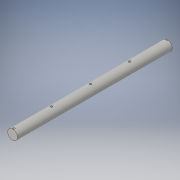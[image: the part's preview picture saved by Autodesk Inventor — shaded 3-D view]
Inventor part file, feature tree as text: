
AUTODESK INVENTOR PART (.ipt)
format: ipt  version: 2016 (Build 200138000, 138)  size: 129,536 bytes
history: native  units: in
note: dims shown in document units (in); Inventor stores cm internally (conversion verified against a paired STEP export)
features: extrude x4, sketch x3
ambient origin geometry x8: Origin, YZ Plane, XZ Plane, XY Plane, X Axis, Y Axis, Z Axis, Center Point
bodies: Solid1 (feature_tree)
feature tree (7):
  extrude  "Extrusion1"  Depth=8.0in TaperAngle=0.0deg
  extrude  "Extrusion4"  Depth=0.06in
  extrude  "Extrusion5"  Depth=2.0in TaperAngle=0.0deg
  extrude  "Extrusion6"  Depth=2.0in
  sketch  "Sketch1"  dims[d0=0.5in d1=8.0in d2=0.0in]
  sketch  "Sketch4"  dims[d13=0.06in d15=0.06in]
  sketch  "Sketch6"  dims[d16=0.1in d17=0.6in d18=0.0in d19=0.1in d20=0.06in d21=0.05in d23=1.0in d24=0.0in d25=2.0in d26=0.1in d27=2.0in d28=0.1in d29=2.0in d30=0.1in d31=1.0in d32=0.0in]
